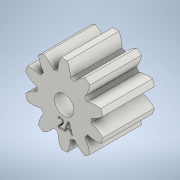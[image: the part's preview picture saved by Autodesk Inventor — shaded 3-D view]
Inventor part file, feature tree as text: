
AUTODESK INVENTOR PART (.ipt)
format: ipt  version: 2021 (Build 250183000, 183)  size: 247,808 bytes
history: native  units: mm (DEFAULTED — no unit token found)
features: sketch x4, plane x3, other x3, extrude x1, hole x1, emboss x1
ambient origin geometry x8: Origin, YZ Plane, XZ Plane, XY Plane, X Axis, Y Axis, Z Axis, Center Point
bodies: Solid1 (feature_tree)
feature tree (13):
  extrude  "Extrusion1"  Depth=8.0mm TaperAngle=0.0deg
  plane  "Work Plane2"
  plane  "Work Plane8"
  plane  "Work Plane9"
  other  "Spur Gear"
  hole  "Hole1"  [1 undecoded]
  emboss  "Emboss1"
  sketch  "Sketch1"  dims[d0=12.303391mm d1=8.0mm d2=0.0mm]
  sketch  "Sketch2"  dims[d3=10.0mm d4=10.0mm d5=0.0mm]
  other  "Srf1"
  sketch  "Sketch3"  dims[d16=25.351695mm]
  sketch  "Sketch4"  dims[d17=0.0mm d34=3.141593mm d39=0.0mm d41=0.0mm d43=25.351695mm d46=25.351695mm d47=0.0mm d48=0.0mm d49=3.0mm d50=3.0mm d51=6.0mm d52=4.0mm d53=2.0mm d54=90.0deg d55=8.0mm d56=20.594885mm d57=1.0mm d58=0.0mm]
  other  "Pitch Diameter"
note: 1 required parameter value undecoded (feature->parameter linkage not recoverable at this tier; creation-order binding heuristic only, values carry confidence <= 0.55)
